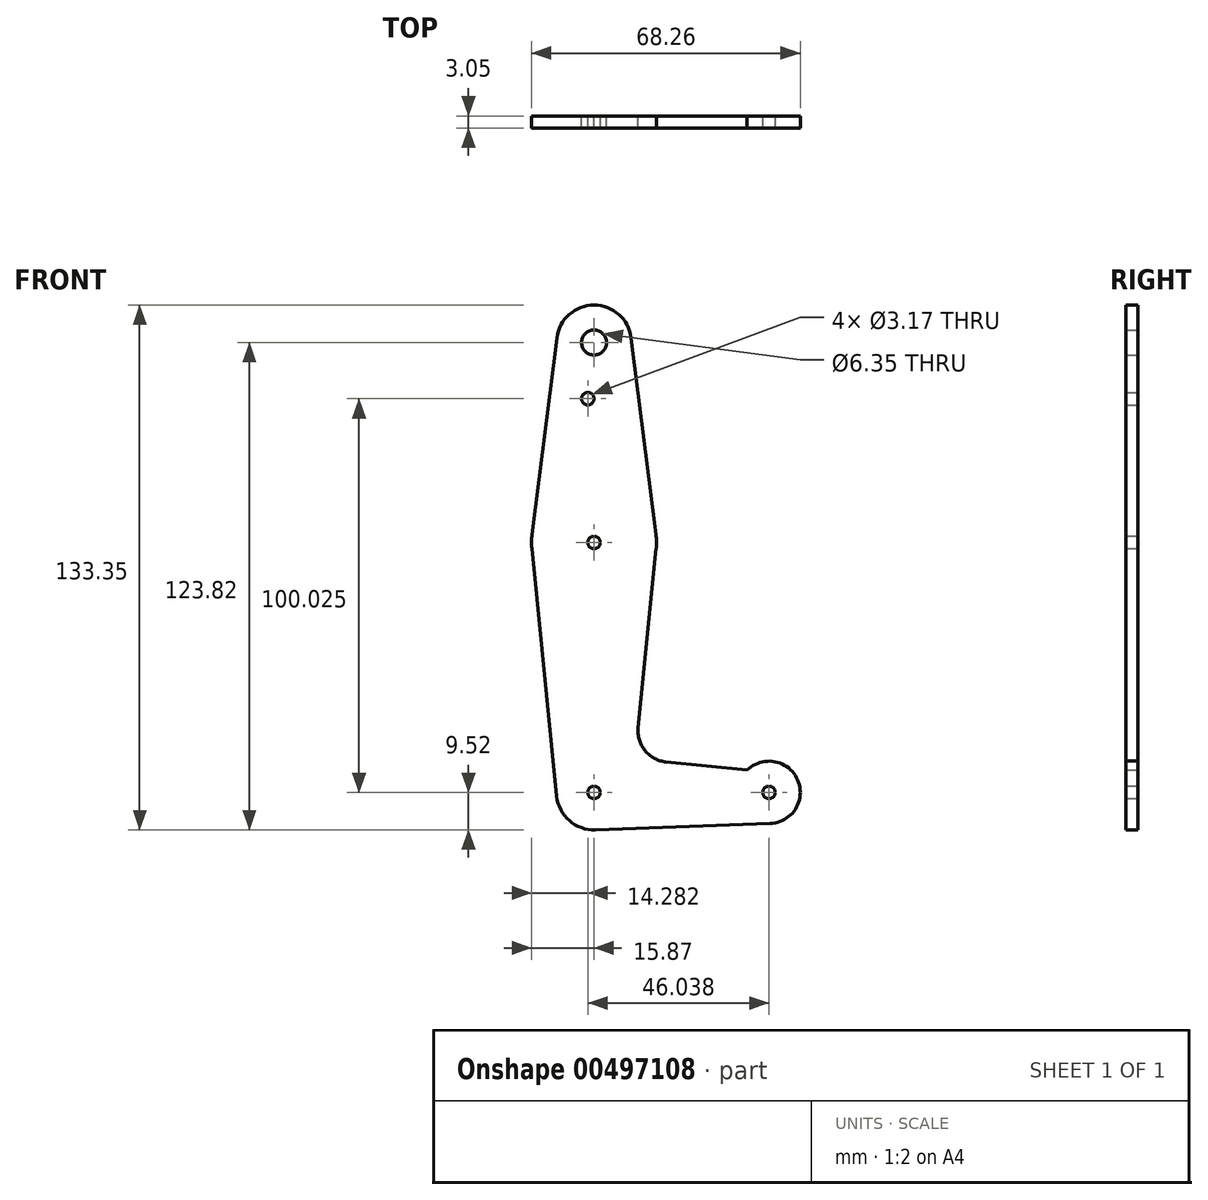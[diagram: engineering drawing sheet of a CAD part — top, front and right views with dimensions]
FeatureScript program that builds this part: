
annotation { "Feature Type Name" : "Feature", "Feature Type Description" : "" }
export const myFeature = defineFeature(function(context is Context, id is Id, definition is map)
    precondition{}
    {
        {
            var Q0;
            Q0=qCreatedBy(makeId("Front.planeOp"),FACE);
            var sketch = newSketch(context, id + "F0", { "sketchPlane" : qUnion([Q0])});
            skLineSegment(sketch, "E0", {"start": v(0, 0) * mm, "end": v(0, 114.3) * mm, "construction": true});
            skLineSegment(sketch, "E1", {"start": v(0, 0) * mm, "end": v(44.45, 0) * mm, "construction": true});
            skCircle(sketch, "E2", {"center": v(0, 0) * mm, "radius": 9.53 * mm});
            skCircle(sketch, "E3", {"center": v(44.45, 0) * mm, "radius": 7.94 * mm});
            skCircle(sketch, "E4", {"center": v(0, 63.5) * mm, "radius": 15.88 * mm});
            skCircle(sketch, "E5", {"center": v(0, 114.3) * mm, "radius": 9.53 * mm});
            skLineSegment(sketch, "E6", {"start": v(-9.45, 115.5) * mm, "end": v(-15.75, 65.48) * mm});
            skLineSegment(sketch, "E7", {"start": v(9.45, 115.5) * mm, "end": v(15.75, 65.48) * mm});
            skLineSegment(sketch, "E8", {"start": v(-15.8, 61.91) * mm, "end": v(-9.48, -0.95) * mm});
            skLineSegment(sketch, "E9", {"start": v(15.8, 61.91) * mm, "end": v(11.22, 16.44) * mm});
            skLineSegment(sketch, "E10", {"start": v(18.34, 7.73) * mm, "end": v(38.89, 5.66) * mm});
            skCircle(sketch, "E11", {"center": v(0, 114.3) * mm, "radius": 3.18 * mm});
            skCircle(sketch, "E12", {"center": v(-1.59, 100.03) * mm, "radius": 1.59 * mm});
            skCircle(sketch, "E13", {"center": v(0, 63.5) * mm, "radius": 1.59 * mm});
            skCircle(sketch, "E14", {"center": v(0, 0) * mm, "radius": 1.59 * mm});
            skCircle(sketch, "E15", {"center": v(44.45, 0) * mm, "radius": 1.59 * mm});
            skLineSegment(sketch, "E16", {"start": v(0.34, -9.52) * mm, "end": v(44.73, -7.93) * mm});
            skArc(sketch, "E17.filletArc", {"start": v(11.22, 16.44) * mm, "mid": v(12.98, 10.6) * mm, "end": v(18.34, 7.73) * mm});
            skSolve(sketch);
        }
        {
            var Q0;
            Q0=makeQuery(id+"F0.imprint","IMPRINT",FACE,{"disambiguationData":[TD([[makeQuery(id+"F0.imprint","IMPRINT",EDGE,{"derivedFrom":sQuery(id+"F0.wireOp",EDGE,"E13")}),-1.0]])]});
            var Q1;
            {var subQ1=sQuery(id+"F0.wireOp",EDGE,"E6");Q1=makeQuery(id+"F0.imprint","IMPRINT",FACE,{"disambiguationData":[TD([[makeQuery(id+"F0.imprint","IMPRINT",EDGE,{"derivedFrom":subQ1}),1.0]])]});}
            var Q2;
            Q2=makeQuery(id+"F0.imprint","IMPRINT",FACE,{"disambiguationData":[TD([[makeQuery(id+"F0.imprint","IMPRINT",EDGE,{"derivedFrom":sQuery(id+"F0.wireOp",EDGE,"E11")}),-1.0]])]});
            var Q3;
            {var subQ0=sQuery(id+"F0.wireOp",EDGE,"E8");Q3=makeQuery(id+"F0.imprint","IMPRINT",FACE,{"disambiguationData":[TD([[makeQuery(id+"F0.imprint","IMPRINT",EDGE,{"derivedFrom":subQ0}),1.0]])]});}
            var Q4;
            Q4=makeQuery(id+"F0.imprint","IMPRINT",FACE,{"disambiguationData":[TD([[makeQuery(id+"F0.imprint","IMPRINT",EDGE,{"derivedFrom":sQuery(id+"F0.wireOp",EDGE,"E14")}),-1.0]])]});
            var Q5;
            Q5=makeQuery(id+"F0.imprint","IMPRINT",FACE,{"disambiguationData":[TD([[makeQuery(id+"F0.imprint","IMPRINT",EDGE,{"derivedFrom":sQuery(id+"F0.wireOp",EDGE,"E15")}),-1.0]])]});
            extrude(context, id + "F1", {"entities" : qUnion([Q0, Q1, Q2, Q3, Q4, Q5]), "depth" : 3.05 * mm});
        }
    });
